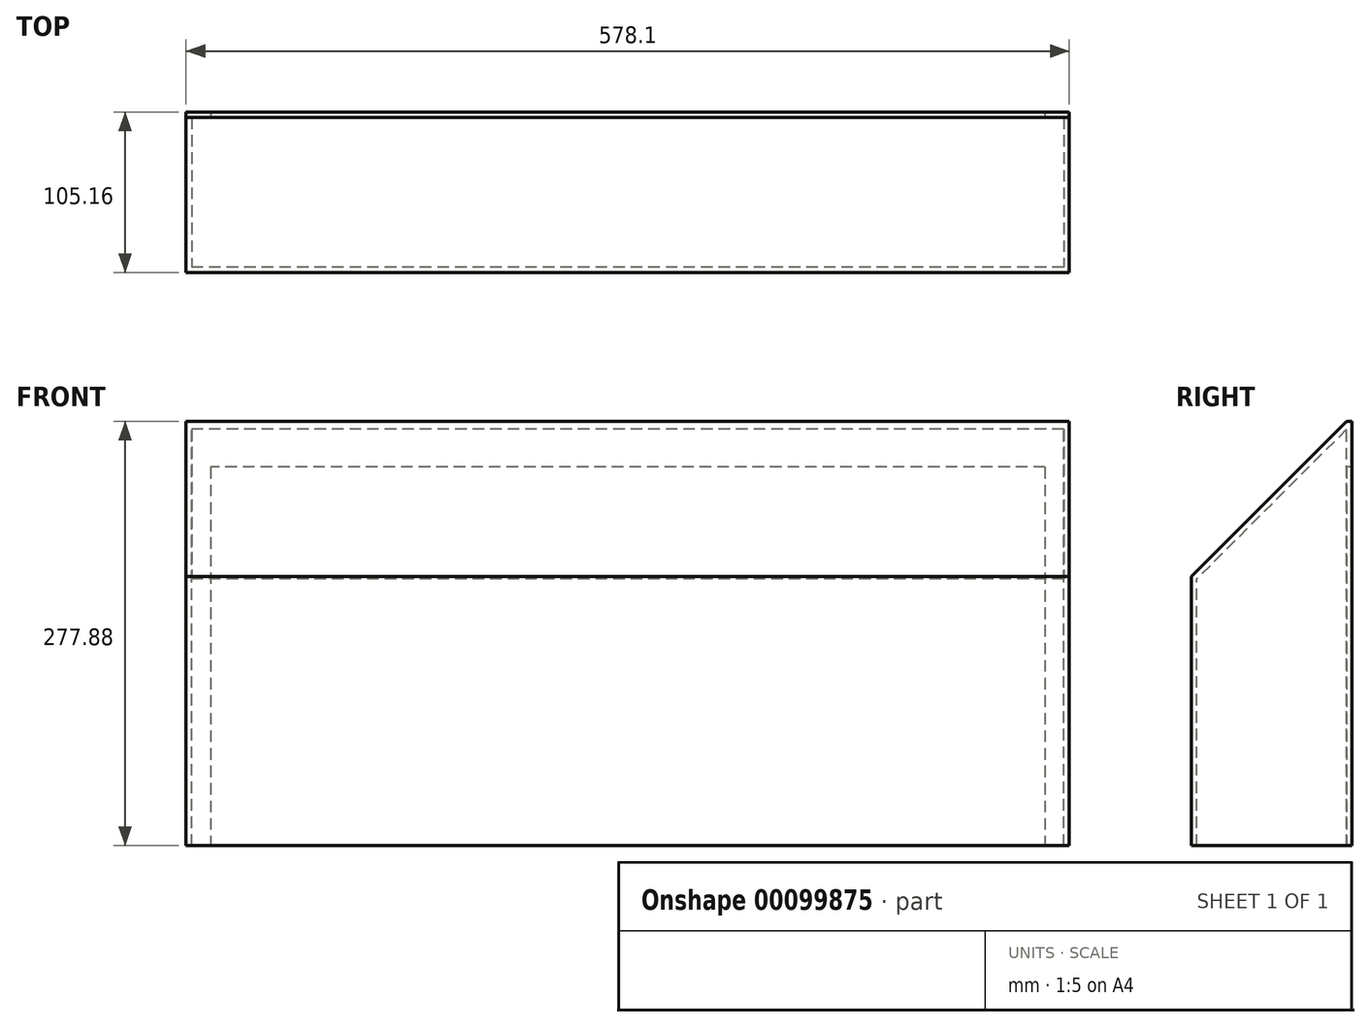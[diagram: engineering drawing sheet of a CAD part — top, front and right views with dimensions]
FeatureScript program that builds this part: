
annotation { "Feature Type Name" : "Feature", "Feature Type Description" : "" }
export const myFeature = defineFeature(function(context is Context, id is Id, definition is map)
    precondition{}
    {
        {
            var Q0;
            Q0=qCreatedBy(makeId("Right.planeOp"),FACE);
            var sketch = newSketch(context, id + "F0", { "sketchPlane" : qUnion([Q0])});
            skLineSegment(sketch, "E0", {"start": v(0, 0) * mm, "end": v(0, 277.88) * mm});
            skLineSegment(sketch, "E1", {"start": v(0, 277.88) * mm, "end": v(-101.6, 176.28) * mm});
            skLineSegment(sketch, "E2", {"start": v(0, 0) * mm, "end": v(-101.6, 0) * mm});
            skLineSegment(sketch, "E3", {"start": v(-101.6, 0) * mm, "end": v(-101.6, 176.28) * mm});
            skSolve(sketch);
        }
        {
            var Q0;
            Q0=qSketchRegion(id+"F0",true);
            extrude(context, id + "F1", {"entities" : qUnion([Q0]), "endBound" : BoundingType.SYMMETRIC, "depth" : 578.1 * mm});
        }
        {
            var Q0;
            Q0=makeQuery(id+"F1.opExtrude","SWEPT_FACE",FACE,{"disambiguationData":[OSD([sQuery(id+"F0.wireOp",EDGE,"E0")])]});
            var Q1;
            Q1=makeQuery(id+"F1.opExtrude","SWEPT_FACE",FACE,{"disambiguationData":[OSD([sQuery(id+"F0.wireOp",EDGE,"E2")])]});
            shell(context, id + "F2", {"entities" : qUnion([Q0, Q1]), "thickness" : 3.56 * mm});
        }
        {
            var Q0;
            Q0=makeQuery(id+"F1.opExtrude","SWEPT_FACE",FACE,{"disambiguationData":[OSD([sQuery(id+"F0.wireOp",EDGE,"E0")])]});
            var sketch = newSketch(context, id + "F3", { "sketchPlane" : qUnion([Q0])});
            skLineSegment(sketch, "E4.bottom", {"start": v(-289.05, 277.88) * mm, "end": v(289.05, 277.88) * mm});
            skLineSegment(sketch, "E4.top", {"start": v(-289.05, 0) * mm, "end": v(-273.18, 0) * mm});
            skLineSegment(sketch, "E4.left", {"start": v(-289.05, 277.88) * mm, "end": v(-289.05, 0) * mm});
            skLineSegment(sketch, "E4.right", {"start": v(289.05, 277.88) * mm, "end": v(289.05, 0) * mm});
            skLineSegment(sketch, "E5.bottom", {"start": v(-273.18, 247.9) * mm, "end": v(273.05, 247.9) * mm});
            skLineSegment(sketch, "E5.left", {"start": v(-273.18, 247.9) * mm, "end": v(-273.18, 0) * mm});
            skLineSegment(sketch, "E5.right", {"start": v(273.05, 247.9) * mm, "end": v(273.05, 0) * mm});
            skLineSegment(sketch, "E6.trimOffspring", {"start": v(273.05, 0) * mm, "end": v(289.05, 0) * mm});
            skSolve(sketch);
        }
        {
            var Q0;
            Q0=qSketchRegion(id+"F3",true);
            extrude(context, id + "F4", {"entities" : qUnion([Q0]), "operationType" : NewBodyOperationType.ADD, "depth" : 3.56 * mm});
        }
    });
